# Revit family: GPB2-130
name_source: partatom
category: Generic Models
revit_build: Autodesk Revit LT 2016 (Build: 20161004_0715(x64)
units: mm (PartAtom-declared; Revit-internal decimal feet)

## family parameters
Always vertical = Yes
Can host rebar = No
Cut with Voids When Loaded = No
Part Type = Normal
Room Calculation Point = No
Round Connector Dimension = Use Diameter
Shared = No
Work Plane-Based = No

## types (2) — shared parameters
A = 8.882 "
B = 4.88 "
BLADE = AA-326-128
C = 9.75 "
D = 4.392 "
E = 7.5 "
F = 6.75 "
G = 9 "
H = 4.12 "
J = 5 "
K = 3.392 "
L = 5.75 "
MOTOR = 302-5929
Manufacturer = REVERSOMATIC
Model = GPB2-130
URL = http://www.reversomatic.com

## per-type parameters (varying)
| type | HOUSING | RPM | SP/CFM |
| GPB2-130  REVERSO DESIGN | REVERSO | 1500 | .00/127  .05/118  .10/104  .15/88  .20/72 |
| GPB2-130 BF-00 | BF-00 | 850 | .00/65  .05/55  .10/35 |

## geometry (parser evidence)
native form markers: Sweep x3
no freeform markers — native parametric forms only
